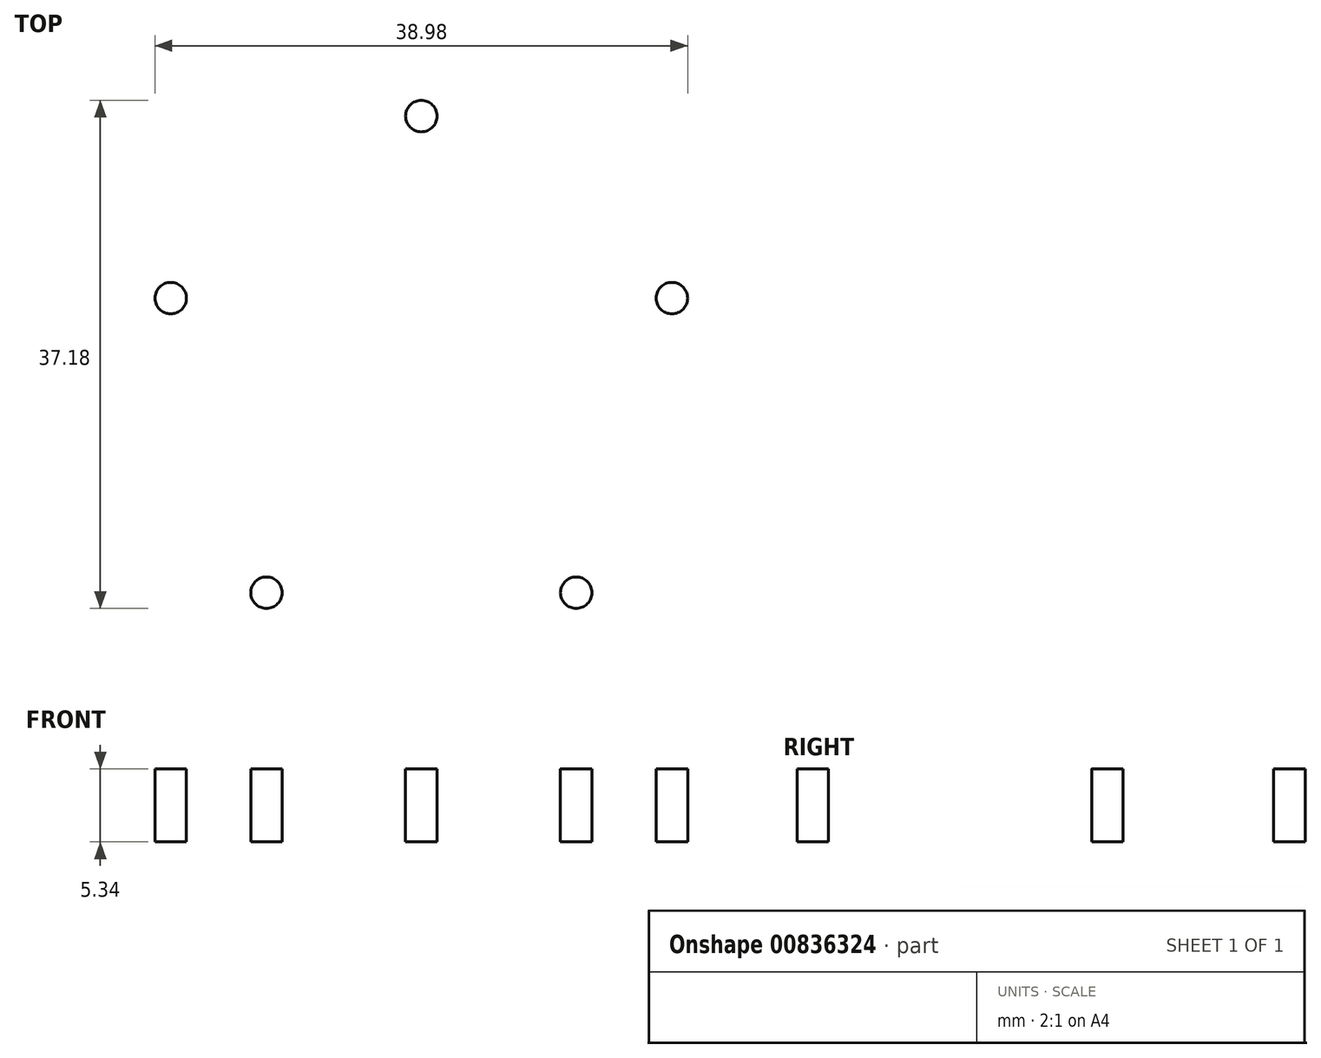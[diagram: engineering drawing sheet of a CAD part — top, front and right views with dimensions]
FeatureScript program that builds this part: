
annotation { "Feature Type Name" : "Feature", "Feature Type Description" : "" }
export const myFeature = defineFeature(function(context is Context, id is Id, definition is map)
    precondition{}
    {
        {
            var Q0;
            Q0=qCreatedBy(makeId("Front.planeOp"),FACE);
            var sketch = newSketch(context, id + "F0", { "sketchPlane" : qUnion([Q0])});
            skLineSegment(sketch, "E0", {"start": v(0, 77.2) * mm, "end": v(0, -74.83) * mm});
            skSolve(sketch);
        }
        {
            var Q0;
            Q0=qCreatedBy(makeId("Top.planeOp"),FACE);
            var sketch = newSketch(context, id + "F1", { "sketchPlane" : qUnion([Q0])});
            skCircle(sketch, "E1", {"center": v(0, 19.28) * mm, "radius": 1.15 * mm});
            skSolve(sketch);
        }
        {
            var Q0;
            Q0=qSketchRegion(id+"F1",true);
            extrude(context, id + "F2", {"entities" : qUnion([Q0]), "endBound" : BoundingType.SYMMETRIC, "depth" : 5.33 * mm, "offsetDistance" : 25.4 * mm});
        }
        {
            var Q0;
            Q0=makeQuery(id+"F2.opExtrude","SWEPT_BODY",BODY,{"disambiguationData":[OSD([sQuery(id+"F1.wireOp",EDGE,"E1")])]});
            var Q1;
            Q1=sQuery(id+"F0.wireOp",EDGE,"E0");
            circularPattern(context, id + "F3", {"entities" : qUnion([Q0]), "axis" : qUnion([Q1]), "angle" : 360 * degree, "instanceCount" : 5, "equalSpace" : true});
        }
    });
